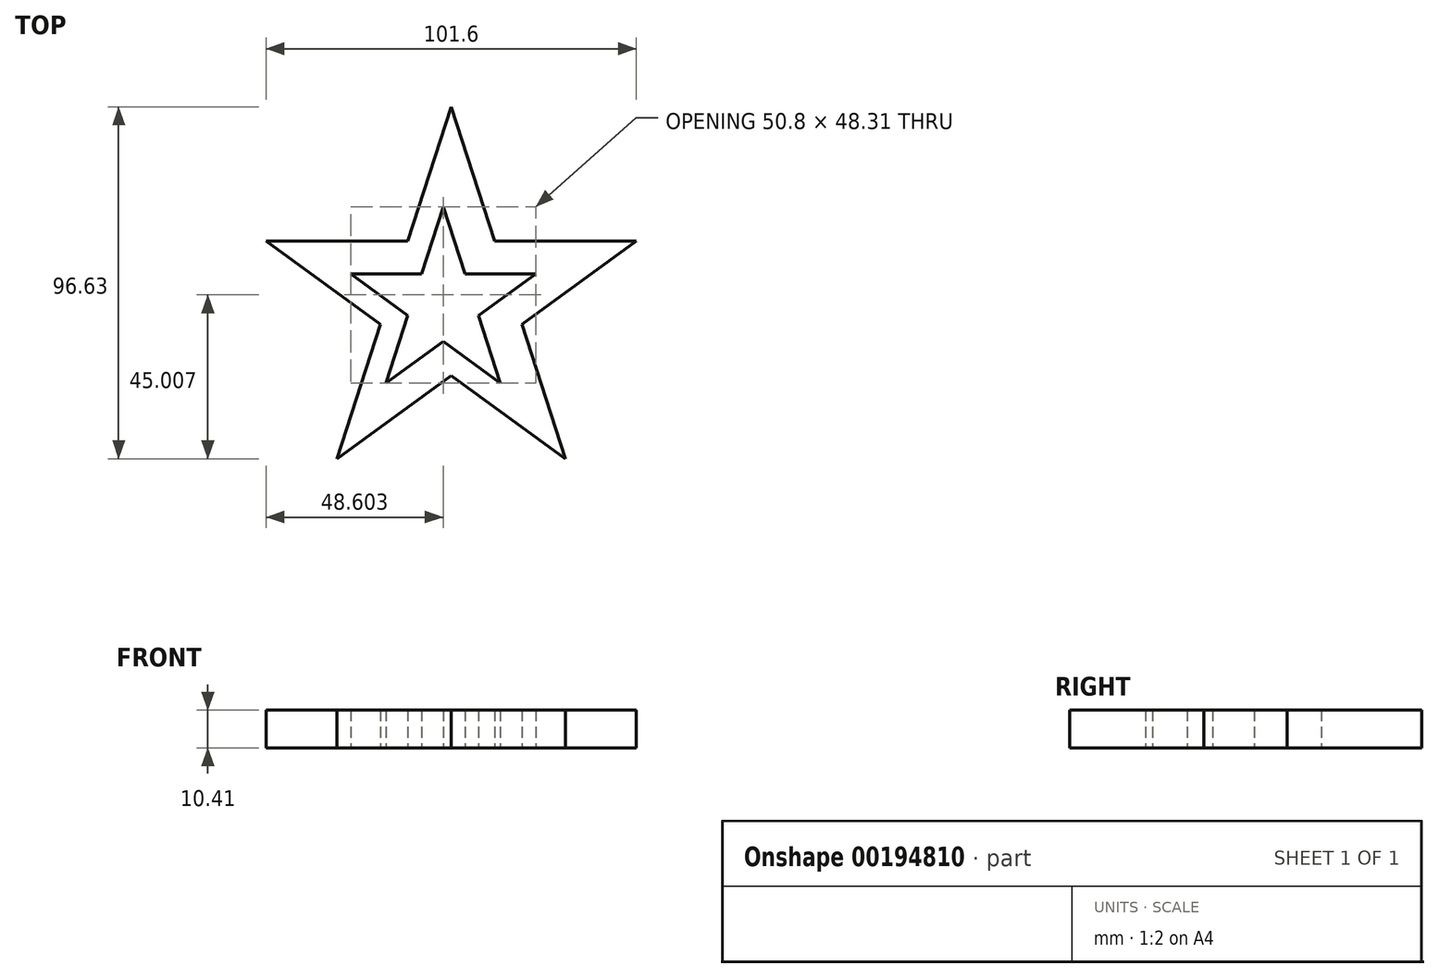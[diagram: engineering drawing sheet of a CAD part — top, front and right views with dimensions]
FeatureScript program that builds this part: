
annotation { "Feature Type Name" : "Feature", "Feature Type Description" : "" }
export const myFeature = defineFeature(function(context is Context, id is Id, definition is map)
    precondition{}
    {
        {
            var Q0;
            Q0=qCreatedBy(makeId("Top.planeOp"),FACE);
            var sketch = newSketch(context, id + "F0", { "sketchPlane" : qUnion([Q0])});
            skLineSegment(sketch, "E0", {"start": v(9.16, 35.08) * mm, "end": v(-6.53, -13.24) * mm});
            skLineSegment(sketch, "E1", {"start": v(-6.53, -13.24) * mm, "end": v(34.56, 16.62) * mm});
            skLineSegment(sketch, "E2", {"start": v(34.56, 16.62) * mm, "end": v(-16.24, 16.62) * mm});
            skLineSegment(sketch, "E3", {"start": v(-16.24, 16.62) * mm, "end": v(24.86, -13.24) * mm});
            skLineSegment(sketch, "E4", {"start": v(9.16, 35.08) * mm, "end": v(24.86, -13.24) * mm});
            skLineSegment(sketch, "E5", {"start": v(-146.43, -19.92) * mm, "end": v(-115.03, 2.9) * mm});
            skLineSegment(sketch, "E6", {"start": v(-64.23, 39.8) * mm, "end": v(-103.04, 39.8) * mm});
            skLineSegment(sketch, "E7", {"start": v(-165.83, 39.8) * mm, "end": v(-134.44, 16.99) * mm});
            skLineSegment(sketch, "E8", {"start": v(-83.64, -19.92) * mm, "end": v(-95.63, 16.99) * mm});
            skLineSegment(sketch, "E9", {"start": v(-115.03, 76.7) * mm, "end": v(-127.03, 39.8) * mm});
            skLineSegment(sketch, "E10", {"start": v(-117.23, 49.24) * mm, "end": v(-123.22, 30.79) * mm});
            skLineSegment(sketch, "E11", {"start": v(-132.93, 0.93) * mm, "end": v(-117.23, 12.34) * mm});
            skLineSegment(sketch, "E12", {"start": v(-91.83, 30.79) * mm, "end": v(-111.23, 30.79) * mm});
            skLineSegment(sketch, "E13", {"start": v(-142.63, 30.79) * mm, "end": v(-126.93, 19.38) * mm});
            skLineSegment(sketch, "E14", {"start": v(-117.23, 49.24) * mm, "end": v(-111.23, 30.79) * mm});
            skLineSegment(sketch, "E15.trimOffspring", {"start": v(-107.53, 19.38) * mm, "end": v(-91.83, 30.79) * mm});
            skLineSegment(sketch, "E16.trimOffspring", {"start": v(-117.23, 12.34) * mm, "end": v(-101.53, 0.93) * mm});
            skLineSegment(sketch, "E17.trimOffspring", {"start": v(-126.93, 19.38) * mm, "end": v(-132.93, 0.93) * mm});
            skLineSegment(sketch, "E18.trimOffspring", {"start": v(-123.22, 30.79) * mm, "end": v(-142.63, 30.79) * mm});
            skLineSegment(sketch, "E19.trimOffspring", {"start": v(-107.53, 19.38) * mm, "end": v(-101.53, 0.93) * mm});
            skLineSegment(sketch, "E20.trimOffspring", {"start": v(-95.63, 16.99) * mm, "end": v(-64.23, 39.8) * mm});
            skLineSegment(sketch, "E21.trimOffspring", {"start": v(-134.44, 16.99) * mm, "end": v(-146.43, -19.92) * mm});
            skLineSegment(sketch, "E22.trimOffspring", {"start": v(-127.03, 39.8) * mm, "end": v(-165.83, 39.8) * mm});
            skLineSegment(sketch, "E23.trimOffspring", {"start": v(-103.04, 39.8) * mm, "end": v(-115.03, 76.7) * mm});
            skLineSegment(sketch, "E24.trimOffspring", {"start": v(-115.03, 2.9) * mm, "end": v(-83.64, -19.92) * mm});
            skSolve(sketch);
        }
        {
            var Q0;
            Q0=makeQuery(id+"F0.imprint","IMPRINT",FACE,{"disambiguationData":[TD([[makeQuery(id+"F0.imprint","IMPRINT",EDGE,{"derivedFrom":sQuery(id+"F0.wireOp",EDGE,"E5")}),1.0]])]});
            extrude(context, id + "F1", {"entities" : qUnion([Q0]), "depth" : 10.4 * mm});
        }
    });
